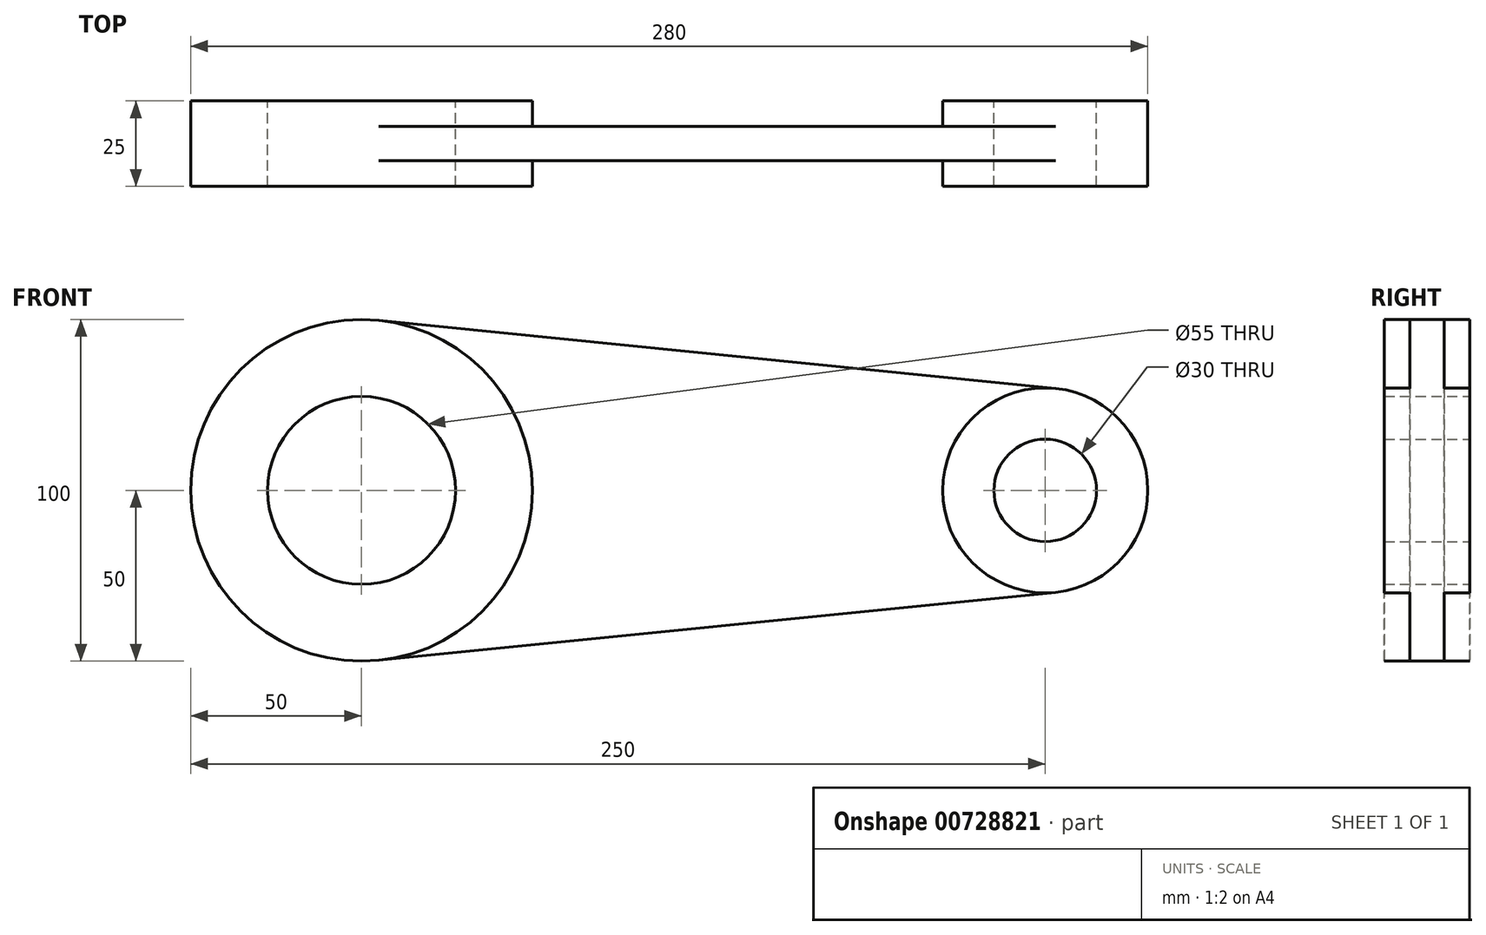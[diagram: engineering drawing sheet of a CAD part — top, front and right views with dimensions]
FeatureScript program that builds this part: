
annotation { "Feature Type Name" : "Feature", "Feature Type Description" : "" }
export const myFeature = defineFeature(function(context is Context, id is Id, definition is map)
    precondition{}
    {
        {
            var Q0;
            Q0=qCreatedBy(makeId("Front.planeOp"),FACE);
            var sketch = newSketch(context, id + "F0", { "sketchPlane" : qUnion([Q0])});
            skCircle(sketch, "E0", {"center": v(-200, 0) * mm, "radius": 27.5 * mm});
            skCircle(sketch, "E1", {"center": v(-200, 0) * mm, "radius": 50 * mm});
            skCircle(sketch, "E2", {"center": v(0, 0) * mm, "radius": 15 * mm});
            skCircle(sketch, "E3", {"center": v(0, 0) * mm, "radius": 30 * mm});
            skLineSegment(sketch, "E4", {"start": v(-195, 49.75) * mm, "end": v(3, 29.85) * mm});
            skLineSegment(sketch, "E5", {"start": v(-195, -49.75) * mm, "end": v(3, -29.85) * mm});
            skSolve(sketch);
        }
        {
            var Q0;
            {var subQ0=sQuery(id+"F0.wireOp",EDGE,"E4");Q0=makeQuery(id+"F0.imprint","IMPRINT",FACE,{"disambiguationData":[TD([[makeQuery(id+"F0.imprint","IMPRINT",EDGE,{"derivedFrom":subQ0}),-1.0]])]});}
            extrude(context, id + "F1", {"entities" : qUnion([Q0]), "endBound" : BoundingType.SYMMETRIC, "depth" : 10 * mm, "offsetDistance" : 25 * mm});
        }
        {
            var Q0;
            Q0=makeQuery(id+"F0.imprint","IMPRINT",FACE,{"disambiguationData":[TD([[makeQuery(id+"F0.imprint","IMPRINT",EDGE,{"derivedFrom":sQuery(id+"F0.wireOp",EDGE,"E0")}),-1.0]])]});
            var Q1;
            Q1=makeQuery(id+"F0.imprint","IMPRINT",FACE,{"disambiguationData":[TD([[makeQuery(id+"F0.imprint","IMPRINT",EDGE,{"derivedFrom":sQuery(id+"F0.wireOp",EDGE,"E2")}),-1.0]])]});
            extrude(context, id + "F2", {"entities" : qUnion([Q0, Q1]), "operationType" : NewBodyOperationType.ADD, "endBound" : BoundingType.SYMMETRIC, "depth" : 25 * mm, "offsetDistance" : 25 * mm});
        }
    });
